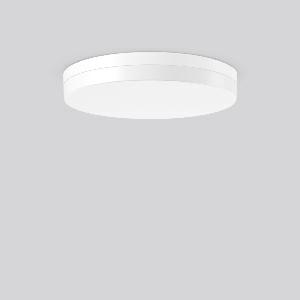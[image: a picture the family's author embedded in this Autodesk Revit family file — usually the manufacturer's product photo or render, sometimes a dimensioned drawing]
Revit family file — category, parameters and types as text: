
# Revit family: flat_slim_round_312634_002_1_26f2
name_source: partatom
category: Lighting Fixtures
units: mm (PartAtom-declared; Revit-internal decimal feet)

## family parameters
Cut with Voids When Loaded = No
Host = Face
Light Source = No
Part Type = Normal
Room Calculation Point = No
Round Connector Dimension = Use Diameter
Shared = No

## types (1)
- MultiLumen 1 830 (1 x LED Modul 830, 3500 lm, 3000)
    Apparent Load = 24 VA
    CIE Flux Codes = 38 68 89 85 100
    Color Rendering = 80
    Color Temperature = 3000
    Default Elevation = 1800 mm
    Height = 70 mm
    Lamp = 1 x LED Modul 830
    Lamp Light Flux = 3500 lm
    Lamp count = 1
    Length = 480 mm
    Lifetime = 50000 h
    Luminous efficacy = 146 lm/W
    Manufacturer = RZB
    ModVariant = No
    Model = 312634.002.1
    Mounting Place = Ceiling
    Mounting Type = Surface mounted
    Number of Poles = 1
    OnlyDefault = Yes
    Power Factor = 1
    Product Name = FLAT SLIM round
    Product group = Surface mounted ceiling and wall luminaires
    ProductGroupID = 305
    Protection Class = Protection class I
    Protection Degree = Degree of protection
    RLX_Detail_Level = 1
    RLX_Emergency_Light_Flux = 0 lm
    RLX_Emergency_Type = 0
    RLX_Emergency_Type_DB = No
    RlxData = <blob elided: 21125 chars, md5=508095d7>
    Socket = socket
    Standby Power = 0 W
    System Light Flux = 3500 lm
    System Power = 24 W
    Type Comments = MultiLumen 1 830
    Type Image = 312633.002.jpg
    URL = http://relux.com
    VarID = multilumen_1_830
    Voltage = 0 V
    Weight = 0.00 kg
    Width = 0 mm  [stored 0 ft]

note: [stored X ft] marks values corroborated as IEEE doubles in the binary element streams (Revit-internal decimal feet)

## geometry (parser evidence)
native form markers: Blend x4, Sweep x13
no freeform markers — native parametric forms only
